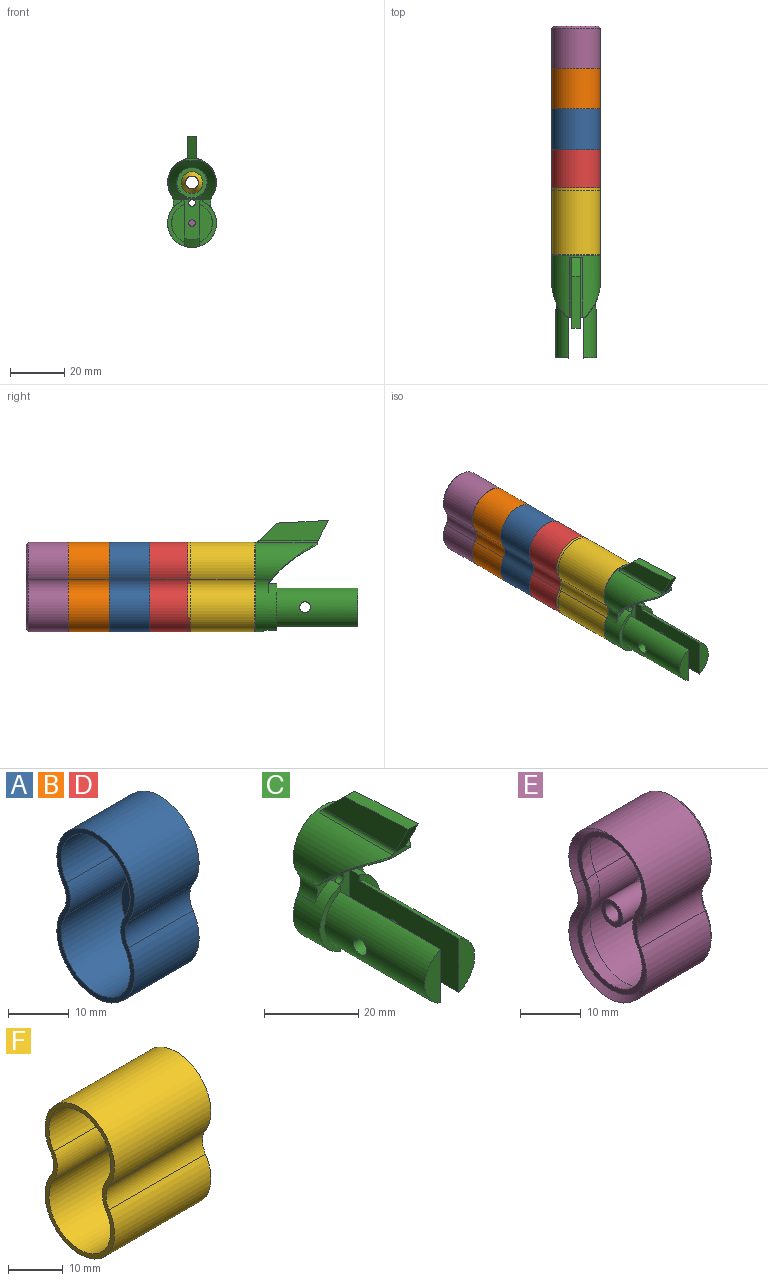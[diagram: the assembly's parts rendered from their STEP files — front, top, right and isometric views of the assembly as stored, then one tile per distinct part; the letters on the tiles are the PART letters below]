
ASSEMBLY  parts=6 mates=5
PART A: 16 faces, bbox 15x18x33 mm
  f0: cylinder r=5mm len=15mm, axis (-1,0,0), area 84.8mm2, adj f1,f3,f5,f6
  f1: cylinder r=9mm len=18mm, axis (-1,0,0), area 576.8mm2, adj f0,f2,f5,f6
  f2: cylinder r=5mm len=15mm, axis (-1,0,0), area 84.8mm2, adj f1,f3,f5,f6
  f3: cylinder r=9mm len=18mm, axis (-1,0,0), area 576.8mm2, adj f0,f2,f5,f6
  f4: cylinder r=2.38mm len=4.75mm, axis (-1,0,0), area 22.4mm2, adj f12,f13
  f5: plane 33x18mm, normal (-1,0,0), area 85.1mm2, adj f0,f1,f2,f3,f8,f9,f10,f11
  f6: plane 33x18mm, normal (1,0,0), area 410.1mm2, adj f0,f1,f2,f3,f13,f14,f15
  f7: plane 31x16mm, normal (-1,0,0), area 316.3mm2, adj f8,f9,f10,f11,f12,f14,f15
  f8: cylinder r=8mm len=16mm, axis (-1,0,0), area 478.5mm2, adj f5,f7,f9,f10
  f9: cylinder r=6mm len=14mm, axis (-1,0,0), area 95mm2, adj f5,f7,f8,f11
  f10: cylinder r=6mm len=14mm, axis (-1,0,0), area 95mm2, adj f5,f7,f8,f11
  f11: cylinder r=8mm len=16mm, axis (-1,0,0), area 478.5mm2, adj f5,f7,f9,f10
  f12: cone r=2.38mm half-angle=30deg, axis (1,0,0), area 120mm2, adj f4,f7
  f13: cone r=2.38mm half-angle=30deg, axis (1,0,0), area 102.4mm2, adj f4,f6
  f14: cylinder r=1.6mm len=3.2mm, axis (1,0,0), area 10.1mm2, adj f6,f7
  f15: cylinder r=1.6mm len=3.2mm, axis (1,0,0), area 10.1mm2, adj f6,f7
PART B: same geometry as A
PART C: 36 faces, bbox 18.5x38.5x41.5 mm
  f0: cylinder r=4mm len=8mm, axis (0,1,0), area 75.4mm2, adj f10,f30
  f1: plane 6.97x1.47mm, normal (0,-1,0), area 5.4mm2, adj f7,f20,f26,f28,f29,f31,f32
  f2: plane 16.22x15.24mm, normal (0,-1,0), area 81.8mm2, adj f6,f7,f8,f9,f14,f15,f16,f20
  f3: plane 17.14x6.25mm, normal (0,-1,0), area 30.5mm2, adj f4,f9,f15
  f4: cylinder r=7.5mm len=30mm, axis (0,1,0), area 525.2mm2, adj f3,f5,f15,f17
  f5: plane 13.96x4.75mm, normal (0,-1,0), area 48.1mm2, adj f4,f15
  f6: cylinder r=5mm len=5.36mm, axis (0,1,0), area 28.3mm2, adj f2,f7,f9,f10
  f7: cylinder r=9mm len=23mm, axis (0,1,0), area 500.8mm2, adj f1,f2,f6,f8,f10,f21,f24,f27
  f8: cylinder r=5mm len=5.36mm, axis (0,1,0), area 28.3mm2, adj f2,f7,f9,f10
  f9: cylinder r=9mm len=18mm, axis (0,1,0), area 318.7mm2, adj f2,f3,f6,f8,f10,f11,f14,f15
  f10: plane 33x18mm, normal (0,1,0), area 435mm2, adj f0,f6,f7,f8,f9,f34,f35
  f11: plane 17.14x6.25mm, normal (0,-1,0), area 30.5mm2, adj f9,f12,f14
  f12: cylinder r=7.5mm len=30mm, axis (0,1,0), area 525.2mm2, adj f11,f13,f14,f18
  f13: plane 13.96x4.75mm, normal (0,-1,0), area 48.1mm2, adj f12,f14
  f14: plane 34.99x17.4mm, normal (-1,0,0), area 460.3mm2, adj f2,f9,f11,f12,f13,f16,f18
  f15: plane 34.99x17.4mm, normal (1,0,0), area 460.3mm2, adj f2,f3,f4,f5,f9,f16,f17
  f16: cone r=6mm half-angle=60deg, axis (0,1,0), area 20.2mm2, adj f2,f9,f14,f15
  f17: cylinder r=2mm len=4.48mm, axis (1,0,0), area 56.3mm2, adj f4,f15
  f18: cylinder r=2mm len=4.48mm, axis (1,0,0), area 56.3mm2, adj f12,f14
  f19: cylinder r=5.56mm len=15.35mm, axis (0,1,0), area 282.5mm2, adj f30,f33
  f20: cylinder r=50mm len=18mm, axis (1,0,0), area 179.7mm2, adj f1,f2,f31,f32,f33
  f21: plane 2.15x0.29mm, normal (0,1,0), area 0.1mm2, adj f7,f24,f28
  f22: plane 25.39x7.32mm, normal (1,0,0), area 136.4mm2, adj f24,f25,f26,f28
  f23: plane 25.39x7.32mm, normal (-1,0,0), area 136.4mm2, adj f24,f25,f26,f29
  f24: plane 7.05x7.05mm, normal (0,0.71,0.71), area 29.9mm2, adj f7,f21,f22,f23,f25,f27,f28,f29
  f25: plane 19.08x3mm, normal (0,0.05,1), area 57.3mm2, adj f22,f23,f24,f26
  f26: plane 8.03x4.1mm, normal (0,-0.89,-0.45), area 27.1mm2, adj f1,f22,f23,f25,f28,f29
  f27: plane 2.15x0.29mm, normal (0,1,0), area 0.1mm2, adj f7,f24,f29
  f28: cylinder r=1mm len=22.35mm, axis (0,1,0), area 28.9mm2, adj f1,f7,f21,f22,f24,f26
  f29: cylinder r=1mm len=22.35mm, axis (0,1,0), area 28.9mm2, adj f1,f7,f23,f24,f26,f27
  f30: plane 11.13x11.13mm, normal (0,-1,0), area 46.9mm2, adj f0,f19
  f31: bspline ~20.29x15.99mm, area 11.5mm2, adj f1,f2,f7,f20
  f32: bspline ~19.61x15.27mm, area 11.5mm2, adj f1,f2,f7,f20
  f33: bspline ~13.48x11.63mm, area 16.8mm2, adj f19,f20
  f34: cylinder r=1.25mm len=5mm, axis (0,1,0), area 39.3mm2, adj f2,f10
  f35: cylinder r=1.25mm len=5mm, axis (0,1,0), area 39.3mm2, adj f2,f10
PART D: same geometry as A
PART E: 30 faces, bbox 15.8x18x33 mm
  f0: cylinder r=5mm len=15mm, axis (-1,0,0), area 84.8mm2, adj f1,f3,f12,f15
  f1: cylinder r=9mm len=18mm, axis (-1,0,0), area 576.8mm2, adj f0,f2,f14,f17
  f2: cylinder r=5mm len=15mm, axis (-1,0,0), area 84.8mm2, adj f1,f3,f13,f18
  f3: cylinder r=9mm len=18mm, axis (-1,0,0), area 576.8mm2, adj f0,f2,f11,f16
  f4: cylinder r=2.38mm len=4.75mm, axis (-1,0,0), area 29.8mm2, adj f5,f6
  f5: plane 31.4x16.4mm, normal (1,0,0), area 375.7mm2, adj f4,f11,f12,f13,f14,f29
  f6: plane 31x16mm, normal (-1,0,0), area 328.7mm2, adj f4,f7,f8,f9,f10,f26
  f7: cylinder r=8mm len=16mm, axis (-1,0,0), area 334.9mm2, adj f6,f8,f9,f22
  f8: cylinder r=6mm len=9.8mm, axis (-1,0,0), area 66.5mm2, adj f6,f7,f10,f23
  f9: cylinder r=6mm len=9.8mm, axis (-1,0,0), area 66.5mm2, adj f6,f7,f10,f20
  f10: cylinder r=8mm len=16mm, axis (-1,0,0), area 334.9mm2, adj f6,f8,f9,f21
  f11: cone r=8mm half-angle=45deg, axis (-1,0,0), area 41.6mm2, adj f3,f5,f12,f13
  f12: cone r=6mm half-angle=45deg, axis (1,0,0), area 6.9mm2, adj f0,f5,f11,f14
  f13: cone r=6mm half-angle=45deg, axis (1,0,0), area 6.9mm2, adj f2,f5,f11,f14
  f14: cone r=8mm half-angle=45deg, axis (-1,0,0), area 41.6mm2, adj f1,f5,f12,f13
  f15: cone r=6mm half-angle=45deg, axis (1,0,0), area 8.8mm2, adj f0,f16,f17,f19
  f16: cone r=8mm half-angle=45deg, axis (-1,0,0), area 51.4mm2, adj f3,f15,f18,f19
  f17: cone r=8mm half-angle=45deg, axis (-1,0,0), area 51.4mm2, adj f1,f15,f18,f19
  f18: cone r=6mm half-angle=45deg, axis (1,0,0), area 8.8mm2, adj f2,f16,f17,f19
  f19: plane 31x16mm, normal (-1,0,0), area 78.8mm2, adj f15,f16,f17,f18,f20,f21,f22,f23
  f20: cone r=6mm half-angle=18.4deg, axis (-1,0,0), area 23.2mm2, adj f9,f19,f21,f22
  f21: cone r=8mm half-angle=18.4deg, axis (1,0,0), area 101.3mm2, adj f10,f19,f20,f23
  f22: cone r=8mm half-angle=18.4deg, axis (1,0,0), area 101.3mm2, adj f7,f19,f20,f23
  f23: cone r=6mm half-angle=18.4deg, axis (-1,0,0), area 23.2mm2, adj f8,f19,f21,f22
  f24: plane 5x5mm, normal (-1,0,0), area 11.6mm2, adj f25,f27
  f25: cylinder r=2.5mm len=7.31mm, axis (1,0,0), area 114.7mm2, adj f24,f26
  f26: cone r=2.5mm half-angle=20deg, axis (1,0,0), area 128.6mm2, adj f6,f25
  f27: cylinder r=1.6mm len=11.8mm, axis (1,0,0), area 118.6mm2, adj f24,f28
  f28: plane 6.5x6.5mm, normal (1,0,0), area 25.1mm2, adj f27,f29
  f29: cylinder r=3.25mm len=6.5mm, axis (1,0,0), area 61.3mm2, adj f5,f28
PART F: 16 faces, bbox 25x18x33 mm
  f0: cylinder r=5mm len=25mm, axis (-1,0,0), area 141.3mm2, adj f1,f3,f5,f6
  f1: cylinder r=9mm len=25mm, axis (-1,0,0), area 961.3mm2, adj f0,f2,f5,f6
  f2: cylinder r=5mm len=25mm, axis (-1,0,0), area 141.3mm2, adj f1,f3,f5,f6
  f3: cylinder r=9mm len=25mm, axis (-1,0,0), area 961.3mm2, adj f0,f2,f5,f6
  f4: cylinder r=2.38mm len=4.75mm, axis (-1,0,0), area 14.9mm2, adj f12,f13
  f5: plane 33x18mm, normal (-1,0,0), area 85.1mm2, adj f0,f1,f2,f3,f8,f9,f10,f11
  f6: plane 33x18mm, normal (1,0,0), area 401.3mm2, adj f0,f1,f2,f3,f13,f14,f15
  f7: plane 31x16mm, normal (-1,0,0), area 316.3mm2, adj f8,f9,f10,f11,f12,f14,f15
  f8: cylinder r=8mm len=24mm, axis (-1,0,0), area 820.3mm2, adj f5,f7,f9,f10
  f9: cylinder r=6mm len=24mm, axis (-1,0,0), area 162.8mm2, adj f5,f7,f8,f11
  f10: cylinder r=6mm len=24mm, axis (-1,0,0), area 162.8mm2, adj f5,f7,f8,f11
  f11: cylinder r=8mm len=24mm, axis (-1,0,0), area 820.3mm2, adj f5,f7,f9,f10
  f12: cone r=2.38mm half-angle=30deg, axis (1,0,0), area 120mm2, adj f4,f7
  f13: cone r=2.38mm half-angle=30deg, axis (1,0,0), area 120mm2, adj f4,f6
  f14: cylinder r=1.6mm len=3.2mm, axis (1,0,0), area 10.1mm2, adj f6,f7
  f15: cylinder r=1.6mm len=3.2mm, axis (1,0,0), area 10.1mm2, adj f6,f7
PLACE A rot(axis=(0,0,1),90deg) t=(-15.14,51.41,-6.49)mm
PLACE B rot(axis=(0,0,1),90deg) t=(-15.14,66.41,-6.49)mm
PLACE C t=(-15.14,12.61,-6.49)mm fixed
PLACE D rot(axis=(0,0,1),90deg) t=(-15.14,36.41,-6.49)mm
PLACE E rot(axis=(0,0,1),90deg) t=(-15.14,81.21,-6.49)mm
PLACE F rot(axis=(0,0,1),90deg) t=(-15.14,12.41,-6.49)mm
MATE cylindrical C.f7 <-> E.f3  axis (0,1,0) through (-15.14,1.11,8.51)mm
MATE cylindrical C.f9 <-> E.f1  axis (0,1,0) through (-15.14,8.61,-6.49)mm
MATE cylindrical C.f9 <-> F.f1  axis (0,1,0) through (-15.14,4.61,-6.49)mm
MATE cylindrical D.f1 <-> F.f1  axis (0,-1,0) through (-15.14,43.91,-6.49)mm
MATE cylindrical F.f3 <-> D.f3  axis (0,-1,0) through (-15.14,24.91,8.51)mm
